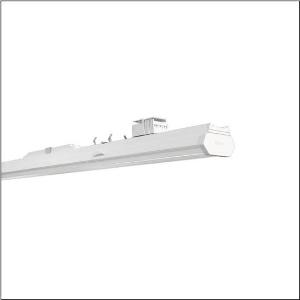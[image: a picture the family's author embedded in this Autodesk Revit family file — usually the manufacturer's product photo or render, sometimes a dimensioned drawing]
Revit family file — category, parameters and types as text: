
# Revit family: licross_r__21_protected_mo_52td12dn4a5g3s4_b622
name_source: partatom
category: Lighting Fixtures
units: mm (PartAtom-declared; Revit-internal decimal feet)

## family parameters
Cut with Voids When Loaded = No
Host = Face
Light Source = No
Part Type = Normal
Room Calculation Point = No
Round Connector Dimension = Use Diameter
Shared = No

## types (1)
- --- (1 x LED, 940 lm, 6.8 W, 4000K)
    Apparent Load = 7 VA
    CIE Flux Codes = 73 92 98 99 100
    Color Rendering = 80
    Color Temperature = 4000K
    Default Elevation = 1800 mm
    Description = Licross® 21 Protected MO, luminaire insert, of sheet steel, galvanised, coil coated, white, length: 1.500mm, width: 90mm, height: 103mm, LED rated luminous flux: 10.700lm, light colour: 840, control gear: DALI 2, with plug, 6-pole, with phase selection, for trunking rail, 9 or 11-core, mains connection: 220..240V, AC, 50/60Hz, rated input power: 66W, for trunking rail, 9-/11-core, halogen-free wiring, for emergency light function, converter,control gear: single battery element, battery: LiFeP04, 9Ah, primary light control with lens, of plastic, primary optical cover: cover, of PMMA, light emission: direct distribution, primary light characteristic: symmetric, protection rating (complete): IP54, insulation class (complete): insulation class I (protective earthing), certification: CE, UKCA, protection symbol: D if used in an environment with non-conductive dust loads with corresponding accessories, impact resistance: IK06, permissible ambient temperature for indoor applications: +5..+35°C, standard: EN 60598-2-22, LABS conformity tested according to VDMA 24364:2018-05, reducing of maximum allowable ambient temperature of 5°C with ceiling mounting, corresponds to IFS (International Featured Standards) requirements for safety and quality in the food industry, packaging unit: 1 piece
    Height = 92 mm
    Lamp = 1 x LED
    Lamp Light Flux = 940 lm
    Lamp Power = 6.8 W
    Lamp count = 1
    Length = 1500 mm
    Luminous efficacy = 138 lm/W
    Manufacturer = Siteco
    ModVariant = No
    Model = 52TD12DN4A5G3S4
    Mounting Place = Ceiling
    Mounting Type = Pendant
    Number of Poles = 1
    OnlyDefault = Yes
    Power Factor = 1
    Product Name = Licross® 21 Protected MO
    Product group = luminaire insert
    ProductGroupID = 901
    Protection Class = Protection class I
    Protection Degree = IP 54
    RLX_Detail_Level = 1
    RLX_Emergency_Light_Flux = 0 lm
    RLX_Emergency_Type = 0
    RLX_Emergency_Type_DB = No
    RlxData = <blob elided: 24853 chars, md5=c175afb3>
    Socket = socket
    Standby Power = 0 W
    System Light Flux = 940 lm
    System Power = 7 W
    Type Comments = : emergency light operation: 3 h
    Type Image = l_1256148.jpg
    URL = http://relux.com
    VarID = @adj_059169
    Voltage = 0 V
    Weight = 0.00 kg
    Width = 88 mm

## geometry (parser evidence)
native form markers: Blend x4, Sweep x10
no freeform markers — native parametric forms only
